# Revit family: O62111001_Orinal Petite
name_source: partatom
category: Plumbing Fixtures
units: mm (PartAtom-declared; Revit-internal decimal feet)

## family parameters
Always vertical = Yes
Cut with Voids When Loaded = No
Host = Wall
OmniClass Number = 23.31.21.00
OmniClass Title = Urinals
Part Type = Normal
Room Calculation Point = No
Round Connector Dimension = Use Radius
Shared = No

## types (1)
- Type 1
    Alto = 721 mm  [stored 2.36549 ft]
    Ancho = 270 mm  [stored 0.885827 ft]
    Creado por = IDD
    Description = Orinal ideal para destinos educativos y públicos, de diseño
compacto perfecto para espacios pequeños.
    Dimensiones empacado (H x L x W) = 265 x 325 x 293 mm
    Fecha de creación = 13/08/2020
    Manufacturer = CORONA
    Material = Corona_Porcelana_Sanitaria_Blanco
    Model = Orinal Petite
    Peso Bruto aprox = 7,1 kg. - 15,6 lbs.
    Peso Neto aprox = 6,35 kg. - 14 lbs.
    Profundidad = 237 mm  [stored 0.777559 ft]
    Referencia = 062111001
    URL = https://www.corona.co

note: [stored X ft] marks values corroborated as IEEE doubles in the binary element streams (Revit-internal decimal feet)

## geometry (parser evidence)
native form markers: Sweep x6
no freeform markers — native parametric forms only
